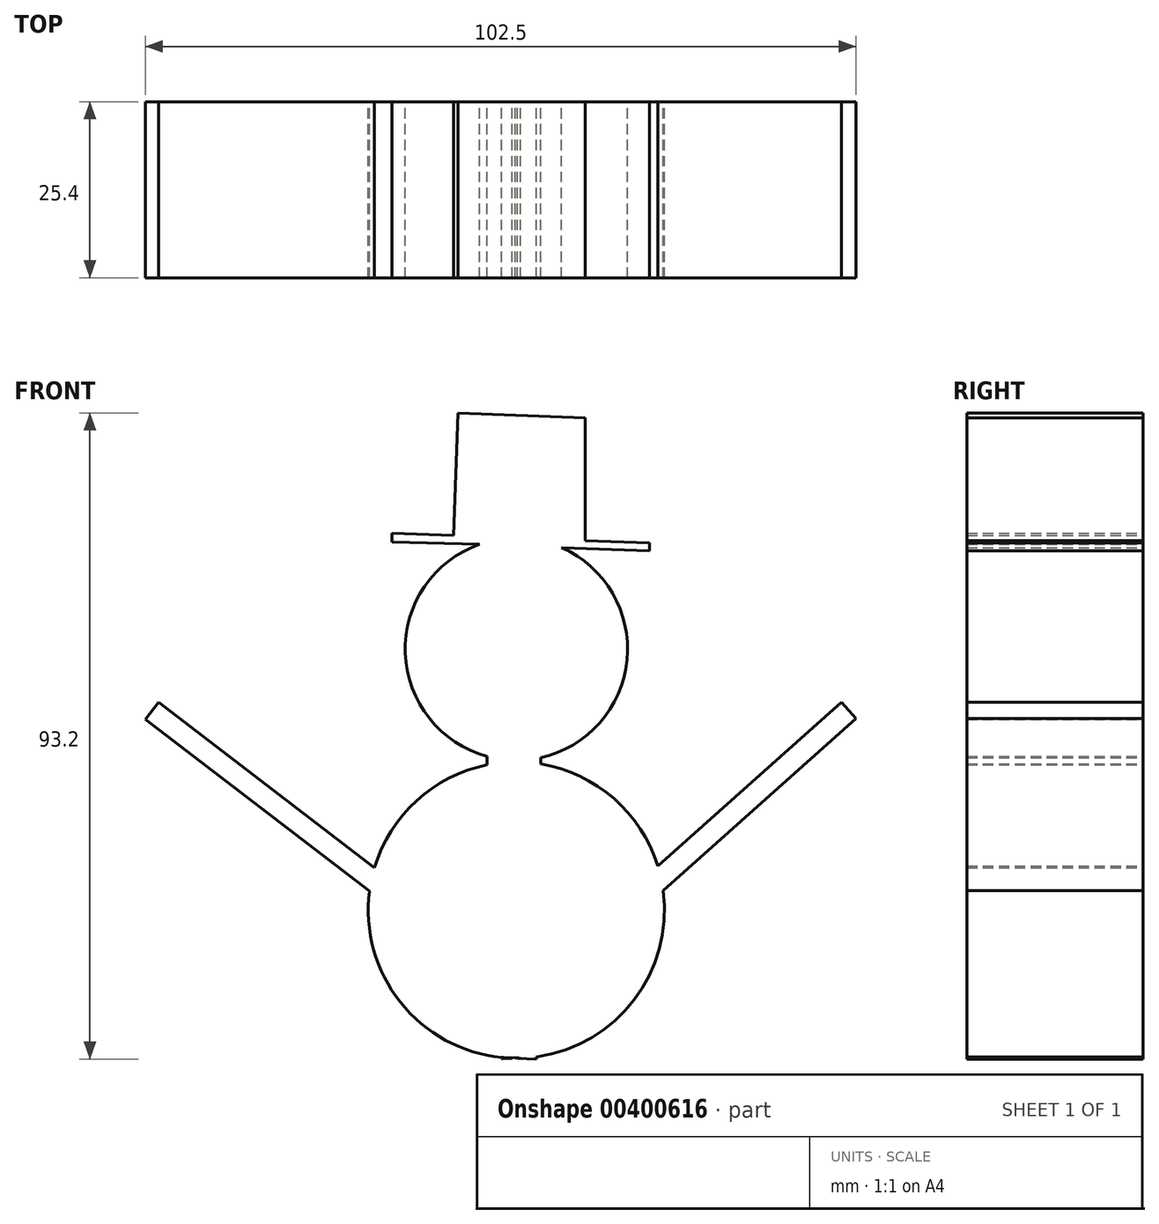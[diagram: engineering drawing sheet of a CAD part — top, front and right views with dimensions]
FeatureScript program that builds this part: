
annotation { "Feature Type Name" : "Feature", "Feature Type Description" : "" }
export const myFeature = defineFeature(function(context is Context, id is Id, definition is map)
    precondition{}
    {
        {
            var Q0;
            Q0=qCreatedBy(makeId("Front.planeOp"),FACE);
            var sketch = newSketch(context, id + "F0", { "sketchPlane" : qUnion([Q0])});
            skCircle(sketch, "E0", {"center": v(0, 0) * mm, "radius": 21.37 * mm});
            skCircle(sketch, "E1", {"center": v(0, -51.24) * mm, "radius": 29.88 * mm});
            skCircle(sketch, "E2", {"center": v(0, 37.64) * mm, "radius": 16.04 * mm});
            skLineSegment(sketch, "E3", {"start": v(-20.48, 6.11) * mm, "end": v(-51.63, 29.95) * mm});
            skLineSegment(sketch, "E4", {"start": v(20.4, 6.35) * mm, "end": v(46.9, 29.95) * mm});
            skLineSegment(sketch, "E5", {"start": v(-17.94, 54.4) * mm, "end": v(19.2, 52.95) * mm});
            skLineSegment(sketch, "E6", {"start": v(-9.08, 54.05) * mm, "end": v(-8.4, 71.7) * mm});
            skLineSegment(sketch, "E7", {"start": v(-8.4, 71.7) * mm, "end": v(9.93, 71) * mm});
            skLineSegment(sketch, "E8", {"start": v(9.93, 71) * mm, "end": v(9.93, 53.3) * mm});
            skLineSegment(sketch, "E9", {"start": v(-51.63, 29.95) * mm, "end": v(-53.51, 27.5) * mm});
            skLineSegment(sketch, "E10", {"start": v(-53.51, 27.5) * mm, "end": v(-21.2, 2.76) * mm});
            skLineSegment(sketch, "E11", {"start": v(46.9, 29.95) * mm, "end": v(49, 27.6) * mm});
            skLineSegment(sketch, "E12", {"start": v(49, 27.6) * mm, "end": v(21.18, 2.83) * mm});
            skLineSegment(sketch, "E13", {"start": v(3.5, 21.08) * mm, "end": v(3.5, 21.98) * mm});
            skLineSegment(sketch, "E14", {"start": v(-4.22, 22.16) * mm, "end": v(-4.22, 20.95) * mm});
            skLineSegment(sketch, "E15", {"start": v(2.87, -21.18) * mm, "end": v(2.87, -21.5) * mm});
            skLineSegment(sketch, "E16", {"start": v(2.87, -21.5) * mm, "end": v(-2.12, -21.27) * mm});
            skLineSegment(sketch, "E17", {"start": v(-2.12, -21.27) * mm, "end": v(-2.12, -21.43) * mm});
            skLineSegment(sketch, "E18", {"start": v(-1.92, 53.77) * mm, "end": v(-1.93, 53.57) * mm});
            skLineSegment(sketch, "E19", {"start": v(3.08, 53.58) * mm, "end": v(3.07, 53.39) * mm});
            skLineSegment(sketch, "E20", {"start": v(19.2, 52.95) * mm, "end": v(19.2, 51.8) * mm});
            skLineSegment(sketch, "E21", {"start": v(19.2, 51.8) * mm, "end": v(6.52, 52.3) * mm});
            skLineSegment(sketch, "E22", {"start": v(-17.94, 54.4) * mm, "end": v(-17.94, 53.09) * mm});
            skLineSegment(sketch, "E23", {"start": v(-17.94, 53.09) * mm, "end": v(-5.3, 52.78) * mm});
            skSolve(sketch);
        }
        {
            var Q0;
            {var subQ0=sQuery(id+"F0.wireOp",EDGE,"E4");Q0=makeQuery(id+"F0.imprint","IMPRINT",FACE,{"disambiguationData":[TD([[makeQuery(id+"F0.imprint","IMPRINT",EDGE,{"derivedFrom":subQ0}),-1.0]])]});}
            var Q1;
            {var subQ0=sQuery(id+"F0.wireOp",EDGE,"E3");Q1=makeQuery(id+"F0.imprint","IMPRINT",FACE,{"disambiguationData":[TD([[makeQuery(id+"F0.imprint","IMPRINT",EDGE,{"derivedFrom":subQ0}),1.0]])]});}
            var Q2;
            {var subQ0=sQuery(id+"F0.wireOp",EDGE,"E13");Q2=makeQuery(id+"F0.imprint","IMPRINT",FACE,{"disambiguationData":[TD([[makeQuery(id+"F0.imprint","IMPRINT",EDGE,{"derivedFrom":subQ0}),1.0]])]});}
            var Q3;
            {var subQ0=sQuery(id+"F0.wireOp",EDGE,"E17");Q3=makeQuery(id+"F0.imprint","IMPRINT",FACE,{"disambiguationData":[TD([[makeQuery(id+"F0.imprint","IMPRINT",EDGE,{"derivedFrom":subQ0}),1.0]])]});}
            var Q4;
            {var subQ0=sQuery(id+"F0.wireOp",EDGE,"E15");Q4=makeQuery(id+"F0.imprint","IMPRINT",FACE,{"disambiguationData":[TD([[makeQuery(id+"F0.imprint","IMPRINT",EDGE,{"derivedFrom":subQ0}),-1.0]])]});}
            var Q5;
            {var subQ1=sQuery(id+"F0.wireOp",EDGE,"E0");var subQ3=sQuery(id+"F0.wireOp",EDGE,"E1");var subQ4=makeQuery(id+"F0.imprint","INTERSECT",VERTEX,{"disambiguationData":[OD(0.0)],"derivedFrom":[subQ1,subQ3]});Q5=makeQuery(id+"F0.imprint","IMPRINT",FACE,{"disambiguationData":[TD([[makeQuery(id+"F0.imprint","IMPRINT",EDGE,{"disambiguationData":[TD([[subQ4,1.0]])],"derivedFrom":subQ3}),-1.0]])]});}
            var Q6;
            {var subQ0=sQuery(id+"F0.wireOp",EDGE,"E1");var subQ1=sQuery(id+"F0.wireOp",EDGE,"E0");var subQ2=makeQuery(id+"F0.imprint","INTERSECT",VERTEX,{"disambiguationData":[OD(0.0)],"derivedFrom":[subQ1,subQ0]});Q6=makeQuery(id+"F0.imprint","IMPRINT",FACE,{"disambiguationData":[TD([[makeQuery(id+"F0.imprint","IMPRINT",EDGE,{"disambiguationData":[TD([[subQ2,-1.0]])],"derivedFrom":subQ1}),-1.0]])]});}
            var Q7;
            {var subQ0=sQuery(id+"F0.wireOp",EDGE,"E16");var subQ1=sQuery(id+"F0.wireOp",EDGE,"E0");var subQ2=makeQuery(id+"F0.imprint","INTERSECT",VERTEX,{"derivedFrom":[subQ1,subQ0]});Q7=makeQuery(id+"F0.imprint","IMPRINT",FACE,{"disambiguationData":[TD([[makeQuery(id+"F0.imprint","IMPRINT",EDGE,{"disambiguationData":[TD([[subQ2,-1.0]])],"derivedFrom":subQ1}),-1.0]])]});}
            var Q8;
            {var subQ3=sQuery(id+"F0.wireOp",EDGE,"E19");Q8=makeQuery(id+"F0.imprint","IMPRINT",FACE,{"disambiguationData":[TD([[makeQuery(id+"F0.imprint","IMPRINT",EDGE,{"derivedFrom":subQ3}),1.0]])]});}
            var Q9;
            {var subQ2=sQuery(id+"F0.wireOp",EDGE,"E18");Q9=makeQuery(id+"F0.imprint","IMPRINT",FACE,{"disambiguationData":[TD([[makeQuery(id+"F0.imprint","IMPRINT",EDGE,{"derivedFrom":subQ2}),-1.0]])]});}
            var Q10;
            {var subQ5=sQuery(id+"F0.wireOp",EDGE,"E6");Q10=makeQuery(id+"F0.imprint","IMPRINT",FACE,{"disambiguationData":[TD([[makeQuery(id+"F0.imprint","IMPRINT",EDGE,{"derivedFrom":subQ5}),-1.0]])]});}
            var Q11;
            {var subQ0=sQuery(id+"F0.wireOp",EDGE,"E0");var subQ4=makeQuery(id+"F0.imprint","INTERSECT",VERTEX,{"derivedFrom":[subQ0,sQuery(id+"F0.wireOp",EDGE,"E4")]});Q11=makeQuery(id+"F0.imprint","IMPRINT",FACE,{"disambiguationData":[TD([[makeQuery(id+"F0.imprint","IMPRINT",EDGE,{"disambiguationData":[TD([[subQ4,1.0]])],"derivedFrom":subQ0}),1.0]])]});}
            var Q12;
            {var subQ0=sQuery(id+"F0.wireOp",EDGE,"E18");Q12=makeQuery(id+"F0.imprint","IMPRINT",FACE,{"disambiguationData":[TD([[makeQuery(id+"F0.imprint","IMPRINT",EDGE,{"derivedFrom":subQ0}),1.0]])]});}
            var Q13;
            {var subQ0=sQuery(id+"F0.wireOp",EDGE,"E19");Q13=makeQuery(id+"F0.imprint","IMPRINT",FACE,{"disambiguationData":[TD([[makeQuery(id+"F0.imprint","IMPRINT",EDGE,{"derivedFrom":subQ0}),-1.0]])]});}
            var Q14;
            {var subQ0=sQuery(id+"F0.wireOp",EDGE,"E2");var subQ4=makeQuery(id+"F0.imprint","INTERSECT",VERTEX,{"derivedFrom":[subQ0,sQuery(id+"F0.wireOp",EDGE,"E19")]});Q14=makeQuery(id+"F0.imprint","IMPRINT",FACE,{"disambiguationData":[TD([[makeQuery(id+"F0.imprint","IMPRINT",EDGE,{"disambiguationData":[TD([[subQ4,1.0]])],"derivedFrom":subQ0}),1.0]])]});}
            extrude(context, id + "F1", {"entities" : qUnion([Q0, Q1, Q2, Q3, Q4, Q5, Q6, Q7, Q8, Q9, Q10, Q11, Q12, Q13, Q14]), "depth" : 25.4 * mm});
        }
    });
